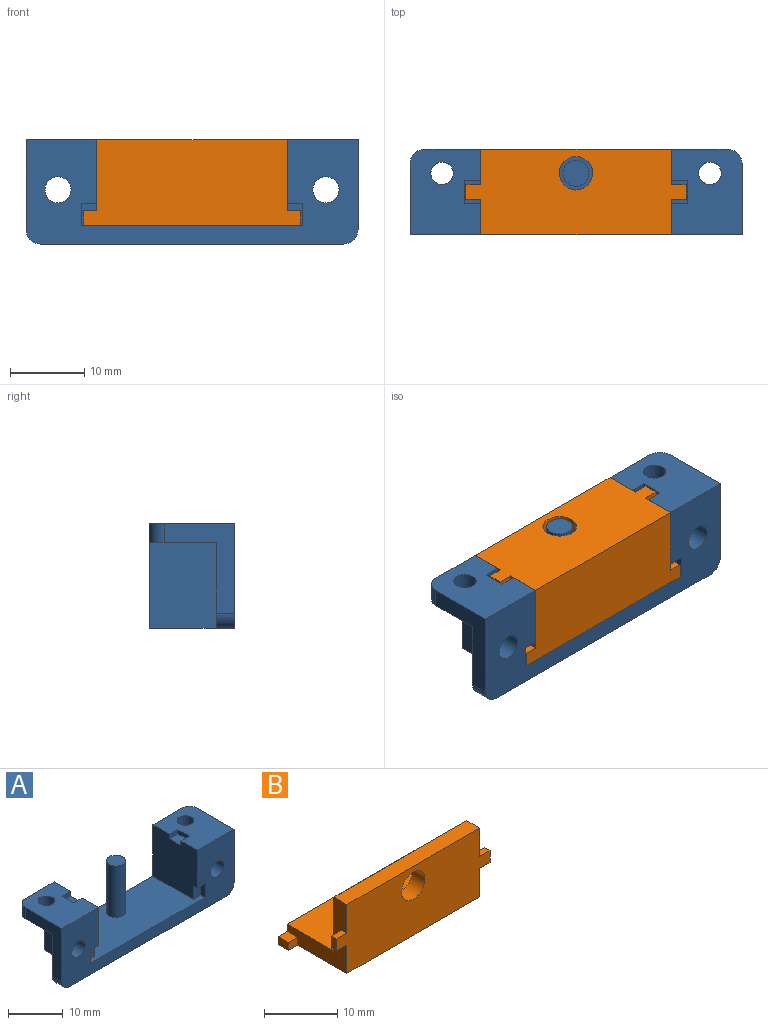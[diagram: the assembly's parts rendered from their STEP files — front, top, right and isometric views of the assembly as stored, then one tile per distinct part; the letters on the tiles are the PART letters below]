
ASSEMBLY  parts=2 mates=1
PART A: 40 faces, bbox 44.6x11.5x14 mm
  f0: plane 11.5x11.5mm, normal (-1,0,0), area 126mm2, adj f2,f7,f8,f10,f26,f28,f36,f38
  f1: plane 11.5x9.5mm, normal (0,0,1), area 94.7mm2, adj f2,f7,f11,f12,f13,f25,f32,f33
  f2: plane 44.6x14mm, normal (0,-1,0), area 297mm2, adj f0,f1,f8,f9,f10,f11,f13,f14
  f3: plane 9x7mm, normal (0,0,-1), area 55.1mm2, adj f5,f7,f14,f15,f21,f24
  f4: plane 9x7mm, normal (0,0,-1), area 55.1mm2, adj f6,f7,f12,f13,f19,f25
  f5: plane 11.5x9mm, normal (1,0,0), area 103.5mm2, adj f3,f7,f9,f21
  f6: plane 11.5x9mm, normal (-1,0,0), area 103.5mm2, adj f4,f7,f9,f19
  f7: plane 40.6x14mm, normal (0,1,0), area 159mm2, adj f0,f1,f3,f4,f5,f6,f8,f9
  f8: plane 29.6x11.5mm, normal (0,0,1), area 289.2mm2, adj f0,f2,f7,f11,f16,f27,f28,f29
  f9: plane 40.6x11.5mm, normal (0,0,-1), area 376.9mm2, adj f2,f5,f6,f7,f19,f21,f22,f23
  f10: plane 11.5x9.5mm, normal (0,0,1), area 94.7mm2, adj f0,f2,f7,f14,f15,f24,f36,f37
  f11: plane 11.5x11.5mm, normal (1,0,0), area 126mm2, adj f1,f2,f7,f8,f30,f31,f32,f34
  f12: cylinder r=1.5mm len=3.01mm, axis (0,0,1), area 23.6mm2, adj f1,f4
  f13: plane 12x9.5mm, normal (-1,0,0), area 47.5mm2, adj f1,f2,f4,f19,f22,f25
  f14: plane 12x9.5mm, normal (1,0,0), area 47.5mm2, adj f2,f3,f10,f21,f23,f24
  f15: cylinder r=1.5mm len=3.01mm, axis (0,0,1), area 23.6mm2, adj f3,f10
  f16: cylinder r=1.75mm len=11.5mm, axis (0,0,-1), area 126.4mm2, adj f8,f17
  f17: plane 3.5x3.5mm, normal (0,0,1), area 9.6mm2, adj f16
  f18: cylinder r=1.75mm len=3.5mm, axis (0,-1,0), area 27.5mm2, adj f2,f19
  f19: plane 11.5x7mm, normal (0,1,0), area 70mm2, adj f4,f6,f9,f13,f18,f22
  f20: cylinder r=1.75mm len=3.5mm, axis (0,-1,0), area 27.5mm2, adj f2,f21
  f21: plane 11.5x7mm, normal (0,1,0), area 70mm2, adj f3,f5,f9,f14,f20,f23
  f22: cylinder r=2mm len=2.5mm, axis (0,1,0), area 7.9mm2, adj f2,f9,f13,f19
  f23: cylinder r=2mm len=2.5mm, axis (0,-1,0), area 7.9mm2, adj f2,f9,f14,f21
  f24: cylinder r=2mm len=2.5mm, axis (0,0,1), area 7.9mm2, adj f3,f7,f10,f14
  f25: cylinder r=2mm len=2.5mm, axis (0,0,-1), area 7.9mm2, adj f1,f4,f7,f13
  f26: plane 2x1.1mm, normal (0,0,-1), area 2.2mm2, adj f0,f2,f27,f28
  f27: plane 3x1.1mm, normal (-1,0,0), area 3.3mm2, adj f2,f8,f26,f28
  f28: plane 3x2mm, normal (0,-1,0), area 6mm2, adj f0,f8,f26,f27
  f29: plane 3x1.1mm, normal (1,0,0), area 3.3mm2, adj f2,f8,f30,f31
  f30: plane 2x1.1mm, normal (0,0,-1), area 2.2mm2, adj f2,f11,f29,f31
  f31: plane 3x2mm, normal (0,-1,0), area 6mm2, adj f8,f11,f29,f30
  f32: plane 2.2x1mm, normal (0,-1,0), area 2.2mm2, adj f1,f11,f33,f35
  f33: plane 3x1mm, normal (1,0,0), area 3mm2, adj f1,f32,f34,f35
  f34: plane 2.2x1mm, normal (0,1,0), area 2.2mm2, adj f1,f11,f33,f35
  f35: plane 3x2.2mm, normal (0,0,1), area 6.6mm2, adj f11,f32,f33,f34
  f36: plane 2.2x1mm, normal (0,1,0), area 2.2mm2, adj f0,f10,f37,f39
  f37: plane 3x1mm, normal (-1,0,0), area 3mm2, adj f10,f36,f38,f39
  f38: plane 2.2x1mm, normal (0,-1,0), area 2.2mm2, adj f0,f10,f37,f39
  f39: plane 3x2.2mm, normal (0,0,1), area 6.6mm2, adj f0,f36,f37,f38
PART B: 23 faces, bbox 29.6x11.5x11.5 mm
  f0: plane 25.6x9mm, normal (0,0,1), area 230.4mm2, adj f3,f6,f7,f10
  f1: plane 1.8x1.3mm, normal (0,-1,0), area 2.3mm2, adj f2,f7,f9,f22
  f2: plane 2x1.3mm, normal (1,0,0), area 2.6mm2, adj f1,f3,f9,f22
  f3: plane 29.2x2.5mm, normal (0,1,0), area 68.7mm2, adj f0,f2,f4,f6,f7,f9,f21,f22
  f4: plane 2x1.3mm, normal (-1,0,0), area 2.6mm2, adj f3,f5,f9,f21
  f5: plane 1.8x1.3mm, normal (0,-1,0), area 2.3mm2, adj f4,f6,f9,f21
  f6: plane 11.5x11.5mm, normal (-1,0,0), area 46.7mm2, adj f0,f3,f5,f8,f9,f10,f11,f12
  f7: plane 11.5x11.5mm, normal (1,0,0), area 46.7mm2, adj f0,f1,f3,f8,f9,f10,f11,f16
  f8: plane 29.6x11.5mm, normal (0,-1,0), area 286.5mm2, adj f6,f7,f9,f11,f12,f13,f14,f16
  f9: plane 29.2x11.5mm, normal (0,0,-1), area 301.6mm2, adj f1,f2,f3,f4,f5,f6,f7,f8
  f10: plane 25.6x9mm, normal (0,1,0), area 214.5mm2, adj f0,f6,f7,f11,f20
  f11: plane 25.6x2.5mm, normal (0,0,1), area 64mm2, adj f6,f7,f8,f10
  f12: plane 2x1mm, normal (0,0,1), area 2mm2, adj f6,f8,f13,f15
  f13: plane 2x1mm, normal (-1,0,0), area 2mm2, adj f8,f12,f14,f15
  f14: plane 2x1mm, normal (0,0,-1), area 2mm2, adj f6,f8,f13,f15
  f15: plane 2x2mm, normal (0,1,0), area 4mm2, adj f6,f12,f13,f14
  f16: plane 2x1mm, normal (0,0,-1), area 2mm2, adj f7,f8,f17,f19
  f17: plane 2x1mm, normal (1,0,0), area 2mm2, adj f8,f16,f18,f19
  f18: plane 2x1mm, normal (0,0,1), area 2mm2, adj f7,f8,f17,f19
  f19: plane 2x2mm, normal (0,1,0), area 4mm2, adj f7,f16,f17,f18
  f20: cylinder r=2.25mm len=4.5mm, axis (0,-1,0), area 35.3mm2, adj f8,f10
  f21: plane 2x1.8mm, normal (0,0,1), area 3.6mm2, adj f3,f4,f5,f6
  f22: plane 2x1.8mm, normal (0,0,1), area 3.6mm2, adj f1,f2,f3,f7
PLACE A t=(-6.01,-5.52,-3.07)mm fixed
PLACE B rot(axis=(-1,0,0),90deg) t=(-18.81,-11.27,8.48)mm
MATE slider A.f16 <-> B.f20  axis (0,0,1) through (-6.01,-3.02,10.93)mm
